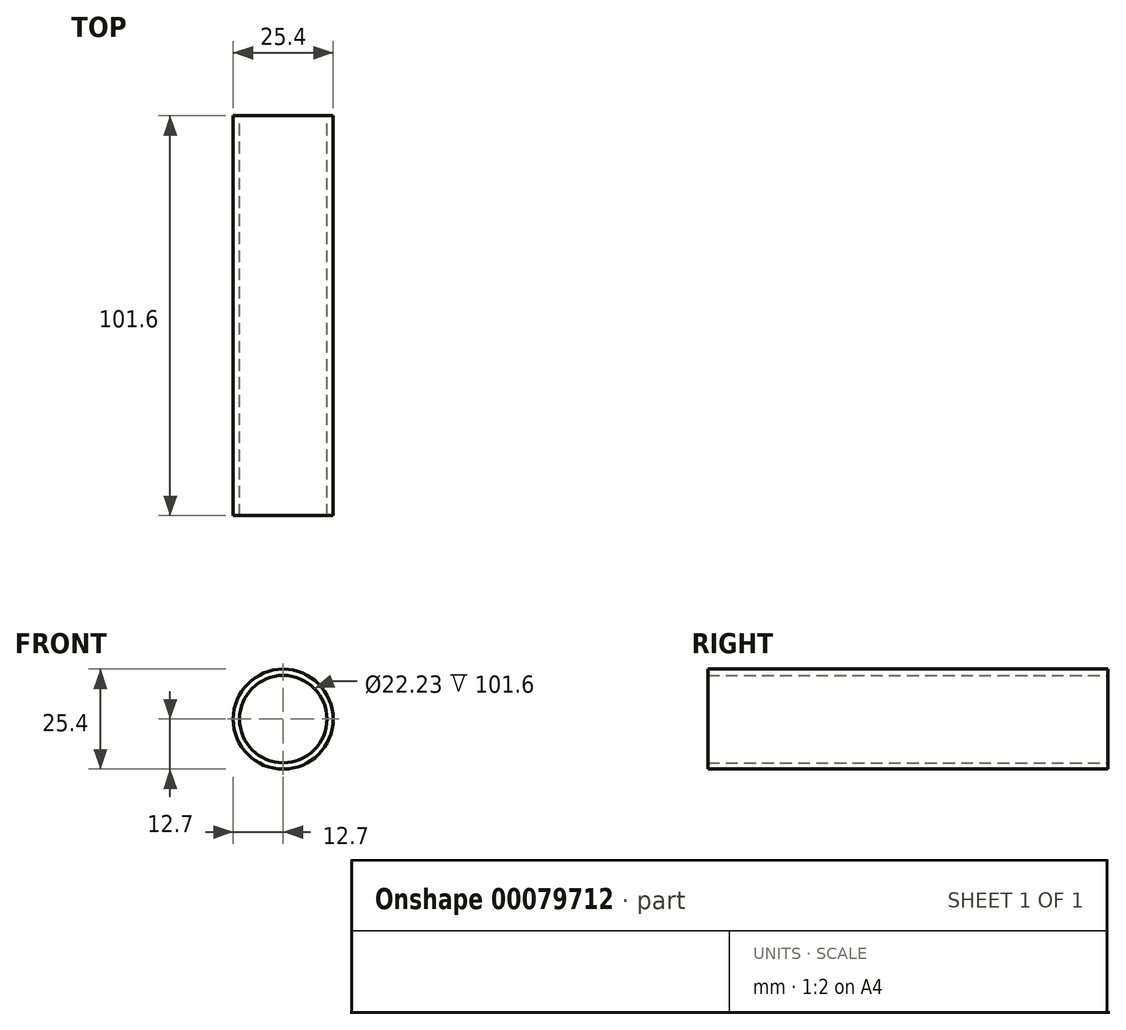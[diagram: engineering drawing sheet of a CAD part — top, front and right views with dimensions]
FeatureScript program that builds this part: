
annotation { "Feature Type Name" : "Feature", "Feature Type Description" : "" }
export const myFeature = defineFeature(function(context is Context, id is Id, definition is map)
    precondition{}
    {
        {
            var Q0;
            Q0=qCreatedBy(makeId("Front.planeOp"),FACE);
            var sketch = newSketch(context, id + "F0", { "sketchPlane" : qUnion([Q0])});
            skCircle(sketch, "E0", {"center": v(0, 0) * mm, "radius": 12.7 * mm});
            skCircle(sketch, "E1", {"center": v(0, 0) * mm, "radius": 11.11 * mm});
            skSolve(sketch);
        }
        {
            var Q0;
            Q0 = qSketchRegion(id + "F0", true);
            extrude(context, id + "F1", {"entities" : qUnion([Q0]), "depth" : 101.6 * mm});
        }
    });
